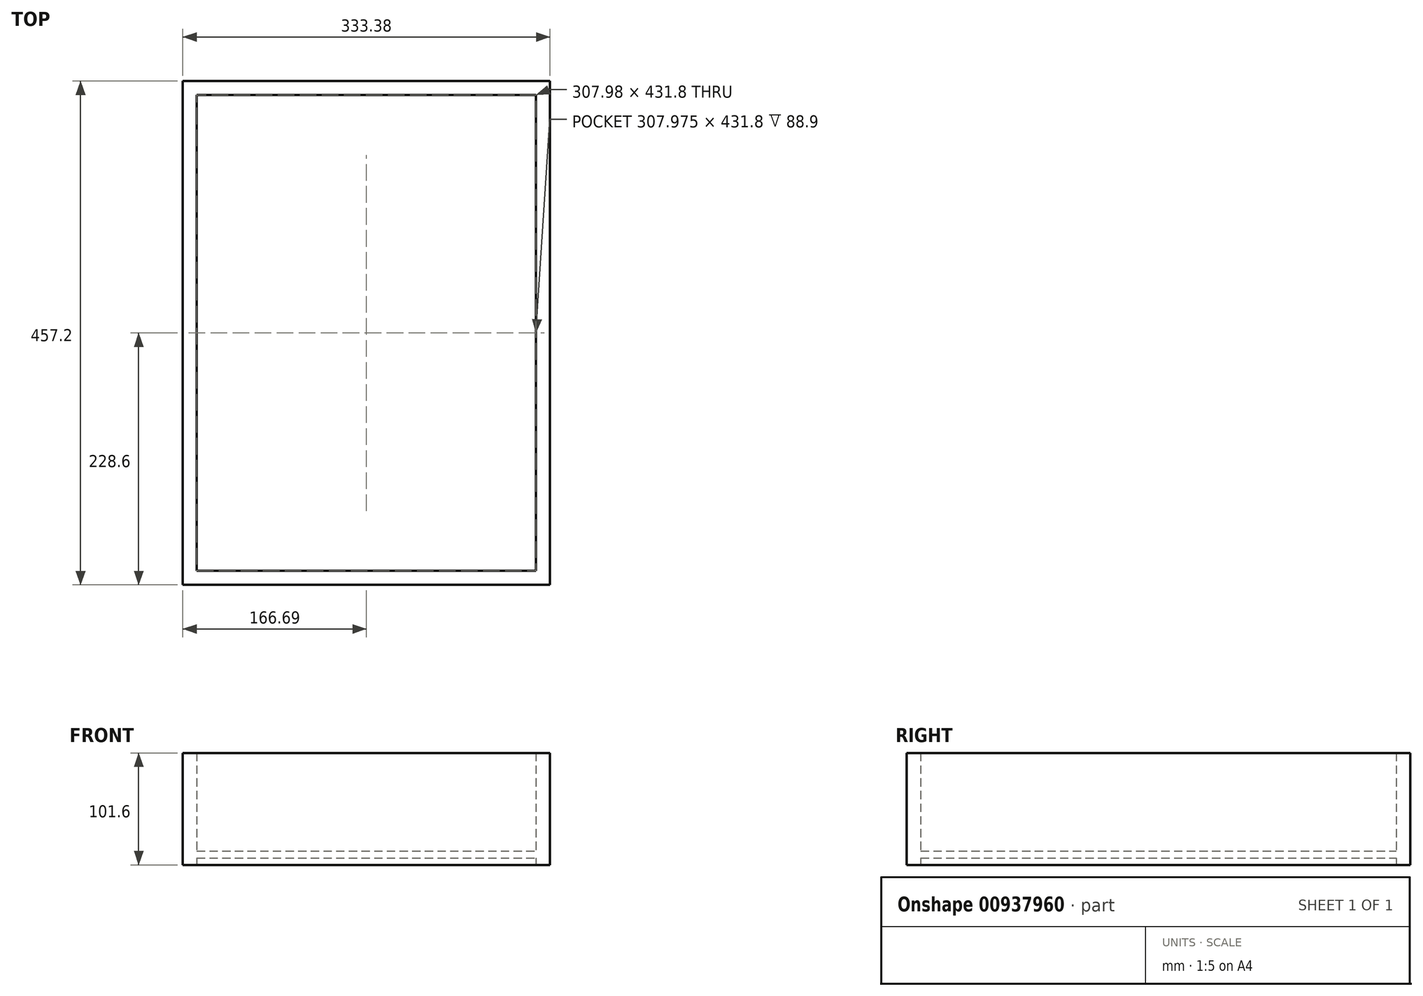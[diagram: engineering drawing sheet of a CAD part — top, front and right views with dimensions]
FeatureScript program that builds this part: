
annotation { "Feature Type Name" : "Feature", "Feature Type Description" : "" }
export const myFeature = defineFeature(function(context is Context, id is Id, definition is map)
    precondition{}
    {
        {
            var Q0;
            Q0=qCreatedBy(makeId("Top.planeOp"),FACE);
            var sketch = newSketch(context, id + "F0", { "sketchPlane" : qUnion([Q0])});
            skLineSegment(sketch, "E0.bottom", {"start": v(166.69, 228.6) * mm, "end": v(-166.69, 228.6) * mm});
            skLineSegment(sketch, "E0.top", {"start": v(166.69, -228.6) * mm, "end": v(-166.69, -228.6) * mm});
            skLineSegment(sketch, "E0.left", {"start": v(166.69, 228.6) * mm, "end": v(166.69, -228.6) * mm});
            skLineSegment(sketch, "E0.right", {"start": v(-166.69, 228.6) * mm, "end": v(-166.69, -228.6) * mm});
            skPoint(sketch, "E0.middle", {"position": v(0, 0) * mm});
            skLineSegment(sketch, "E1.bottom", {"start": v(153.99, 215.9) * mm, "end": v(-153.99, 215.9) * mm});
            skLineSegment(sketch, "E1.top", {"start": v(153.99, -215.9) * mm, "end": v(-153.99, -215.9) * mm});
            skLineSegment(sketch, "E1.left", {"start": v(153.99, 215.9) * mm, "end": v(153.99, -215.9) * mm});
            skLineSegment(sketch, "E1.right", {"start": v(-153.99, 215.9) * mm, "end": v(-153.99, -215.9) * mm});
            skSolve(sketch);
        }
        {
            var Q0;
            Q0=makeQuery(id+"F0.imprint","IMPRINT",FACE,{"disambiguationData":[TD([[makeQuery(id+"F0.imprint","IMPRINT",EDGE,{"derivedFrom":sQuery(id+"F0.wireOp",EDGE,"E0.bottom")}),1.0]])]});
            extrude(context, id + "F1", {"entities" : qUnion([Q0]), "depth" : 101.6 * mm, "offsetDistance" : 25.4 * mm});
        }
        {
            var Q0;
            Q0=makeQuery(id+"F1.opExtrude","SWEPT_FACE",FACE,{"disambiguationData":[OSD([sQuery(id+"F0.wireOp",EDGE,"E1.bottom")])]});
            var sketch = newSketch(context, id + "F2", { "sketchPlane" : qUnion([Q0])});
            skLineSegment(sketch, "E2", {"start": v(-153.99, 0) * mm, "end": v(-153.99, 6.35) * mm});
            skLineSegment(sketch, "E3.bottom", {"start": v(-153.99, 6.35) * mm, "end": v(153.99, 6.35) * mm});
            skLineSegment(sketch, "E3.top", {"start": v(-153.99, 12.7) * mm, "end": v(153.99, 12.7) * mm});
            skLineSegment(sketch, "E3.left", {"start": v(-153.99, 6.35) * mm, "end": v(-153.99, 12.7) * mm});
            skLineSegment(sketch, "E3.right", {"start": v(153.99, 6.35) * mm, "end": v(153.99, 12.7) * mm});
            skSolve(sketch);
        }
        {
            var Q0;
            Q0=makeQuery(id+"F2.imprint","IMPRINT",FACE,{"disambiguationData":[TD([[makeQuery(id+"F2.imprint","IMPRINT",EDGE,{"derivedFrom":sQuery(id+"F2.wireOp",EDGE,"E3.bottom")}),1.0]])]});
            extrude(context, id + "F3", {"entities" : qUnion([Q0]), "operationType" : NewBodyOperationType.ADD, "depth" : 431.8 * mm, "offsetDistance" : 25.4 * mm});
        }
    });
